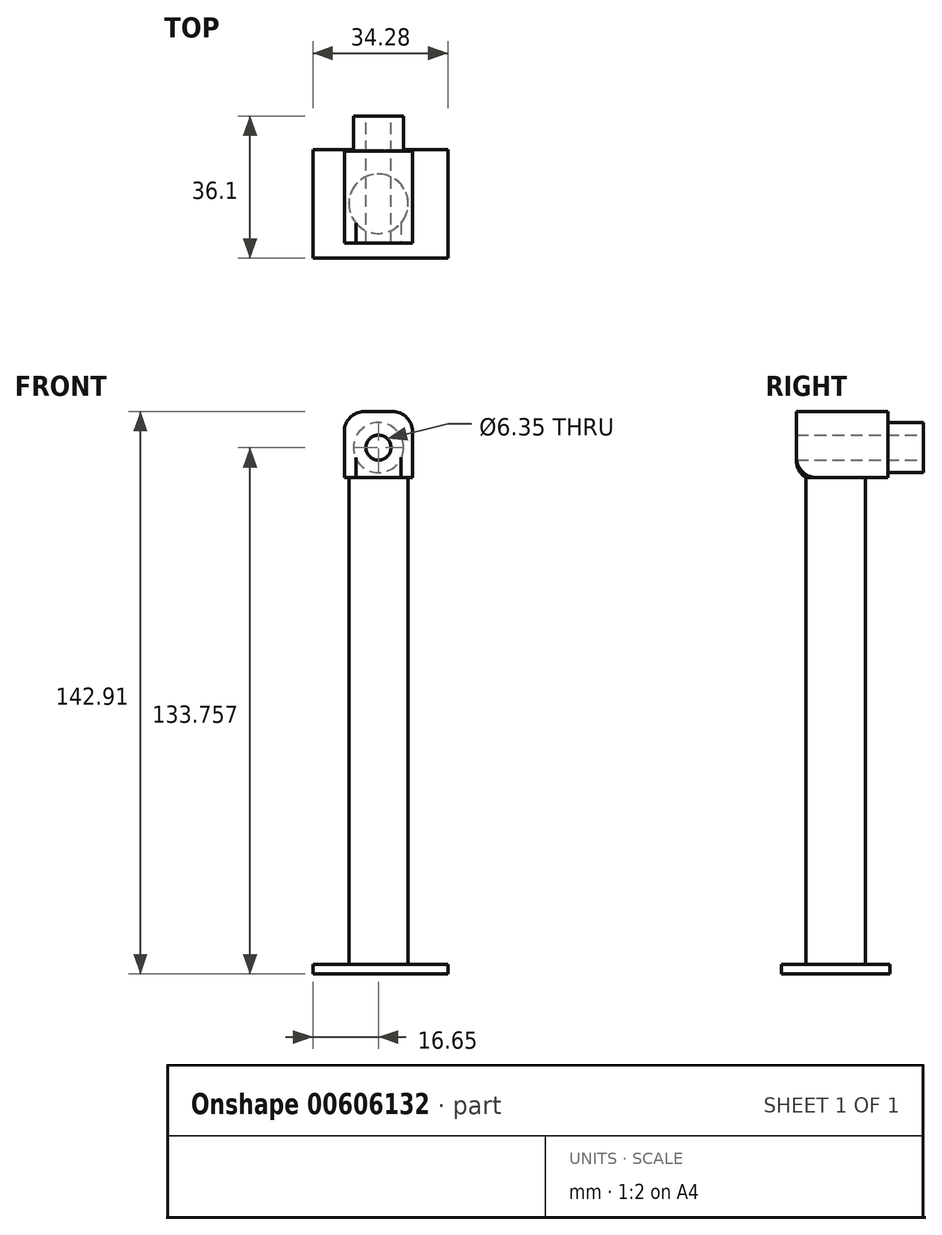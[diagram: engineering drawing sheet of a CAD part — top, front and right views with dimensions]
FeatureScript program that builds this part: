
annotation { "Feature Type Name" : "Feature", "Feature Type Description" : "" }
export const myFeature = defineFeature(function(context is Context, id is Id, definition is map)
    precondition{}
    {
        {
            var Q0;
            Q0=qCreatedBy(makeId("Top.planeOp"),FACE);
            var sketch = newSketch(context, id + "F0", { "sketchPlane" : qUnion([Q0])});
            skLineSegment(sketch, "E0.bottom", {"start": v(-16.65, -13.8) * mm, "end": v(17.63, -13.8) * mm});
            skLineSegment(sketch, "E0.top", {"start": v(-16.65, 13.8) * mm, "end": v(17.63, 13.8) * mm});
            skLineSegment(sketch, "E0.left", {"start": v(-16.65, -13.8) * mm, "end": v(-16.65, 13.8) * mm});
            skLineSegment(sketch, "E0.right", {"start": v(17.63, -13.8) * mm, "end": v(17.63, 13.8) * mm});
            skSolve(sketch);
        }
        {
            var Q0;
            Q0=makeQuery(id+"F0.imprint","IMPRINT",FACE,{"disambiguationData":[TD([[makeQuery(id+"F0.imprint","IMPRINT",EDGE,{"derivedFrom":sQuery(id+"F0.wireOp",EDGE,"E0.bottom")}),1.0]])]});
            extrude(context, id + "F1", {"entities" : qUnion([Q0]), "depth" : 2.47 * mm});
        }
        {
            var Q0;
            Q0=qCreatedBy(makeId("Top.planeOp"),FACE);
            var sketch = newSketch(context, id + "F2", { "sketchPlane" : qUnion([Q0])});
            skCircle(sketch, "E1", {"center": v(0, 0) * mm, "radius": 7.54 * mm});
            skSolve(sketch);
        }
        {
            var Q0;
            Q0=qSketchRegion(id+"F2",true);
            extrude(context, id + "F3", {"entities" : qUnion([Q0]), "operationType" : NewBodyOperationType.ADD, "depth" : 126.15 * mm});
        }
        {
            var Q0;
            Q0=makeQuery(id+"F3.opExtrude","CAP_FACE",FACE,{"disambiguationData":[OSD([sQuery(id+"F2.wireOp",EDGE,"E1")])],"isStart":false});
            var sketch = newSketch(context, id + "F4", { "sketchPlane" : qUnion([Q0])});
            skLineSegment(sketch, "E2.bottom", {"start": v(-8.67, -9.95) * mm, "end": v(8.67, -9.95) * mm});
            skLineSegment(sketch, "E2.top", {"start": v(-8.67, 13.35) * mm, "end": v(8.67, 13.35) * mm});
            skLineSegment(sketch, "E2.left", {"start": v(-8.67, -9.95) * mm, "end": v(-8.67, 13.35) * mm});
            skLineSegment(sketch, "E2.right", {"start": v(8.67, -9.95) * mm, "end": v(8.67, 13.35) * mm});
            skSolve(sketch);
        }
        {
            var Q0;
            Q0=qSketchRegion(id+"F4",true);
            extrude(context, id + "F5", {"entities" : qUnion([Q0]), "operationType" : NewBodyOperationType.ADD, "depth" : 16.76 * mm, "offsetDistance" : 25.4 * mm});
        }
        {
            var Q0;
            Q0=makeQuery(id+"F5.opExtrude","CAP_EDGE",EDGE,{"disambiguationData":[OSD([sQuery(id+"F4.wireOp",EDGE,"E2.left")])],"isStart":false});
            var Q1;
            Q1=makeQuery(id+"F5.opExtrude","CAP_EDGE",EDGE,{"disambiguationData":[OSD([sQuery(id+"F4.wireOp",EDGE,"E2.right")])],"isStart":false});
            fillet(context, id + "F6", {"entities" : qUnion([Q0, Q1]), "radius" : 5.08 * mm, "tangentPropagation" : true, "allowEdgeOverflow" : false});
        }
        {
            var Q0;
            Q0=makeQuery(id+"F5.opExtrude","CAP_EDGE",EDGE,{"disambiguationData":[OSD([sQuery(id+"F4.wireOp",EDGE,"E2.bottom")])],"isStart":true});
            fillet(context, id + "F7", {"entities" : qUnion([Q0]), "radius" : 5.08 * mm, "tangentPropagation" : true, "allowEdgeOverflow" : false});
        }
        {
            var Q0;
            Q0=makeQuery(id+"F5.opExtrude","SWEPT_FACE",FACE,{"disambiguationData":[OSD([sQuery(id+"F4.wireOp",EDGE,"E2.top")])]});
            var sketch = newSketch(context, id + "F8", { "sketchPlane" : qUnion([Q0])});
            skCircle(sketch, "E3", {"center": v(0, 133.76) * mm, "radius": 6.35 * mm});
            skSolve(sketch);
        }
        {
            var Q0;
            Q0=makeQuery(id+"F8.imprint","IMPRINT",FACE,{"disambiguationData":[TD([[makeQuery(id+"F8.imprint","IMPRINT",EDGE,{"derivedFrom":sQuery(id+"F8.wireOp",EDGE,"E3")}),1.0]])]});
            extrude(context, id + "F9", {"entities" : qUnion([Q0]), "operationType" : NewBodyOperationType.ADD, "depth" : 8.94 * mm});
        }
        {
            var Q0;
            Q0=makeQuery(id+"F9.opExtrude","CAP_FACE",FACE,{"disambiguationData":[OSD([sQuery(id+"F8.wireOp",EDGE,"E3")])],"isStart":false});
            var sketch = newSketch(context, id + "F10", { "sketchPlane" : qUnion([Q0])});
            skCircle(sketch, "E4", {"center": v(0, 133.76) * mm, "radius": 3.18 * mm});
            skSolve(sketch);
        }
        {
            var Q0;
            Q0 = qSketchRegion(id + "F10", true);
            extrude(context, id + "F11", {"entities" : qUnion([Q0]), "operationType" : NewBodyOperationType.REMOVE, "oppositeDirection" : true, "depth" : 50.8 * mm, "offsetDistance" : 25.4 * mm});
        }
    });
